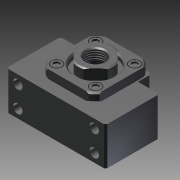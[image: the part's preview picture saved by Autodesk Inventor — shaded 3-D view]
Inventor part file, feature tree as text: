
AUTODESK INVENTOR PART (.ipt)
format: ipt  version: 2011 SP1 (Build 150282100, 282)  size: 373,760 bytes
history: native  units: mm
features: sketch x26, other x14, revolve x12, extrude x9, hole x5, pattern_linear x3, thread x1
ambient origin geometry x8: Origin, YZ Plane, XZ Plane, XY Plane, X Axis, Y Axis, Z Axis, Center Point
bodies: Solid1 (feature_tree)
feature tree (70):
  extrude  "Extrusion1"  Depth=2.5mm TaperAngle=0.0deg
  hole  "Hole1"  [1 undecoded]
  hole  "Hole2"  [1 undecoded]
  hole  "Hole3"  [1 undecoded]
  hole  "Hole4"  [1 undecoded]
  extrude  "Extrusion2"  Depth=20.0mm
  revolve  "Revolution1"  [1 undecoded]
  extrude  "Extrusion3"  Depth=20.0mm
  extrude  "Extrusion4"  TaperAngle=360.0deg  [1 undecoded]
  revolve  "Revolution2"  Angle=360.0deg
  hole  "Hole5"  [1 undecoded]
  revolve  "Revolution3"  Angle=360.0deg
  thread  "Thread1"  [1 undecoded]
  revolve  "Revolution4"  [1 undecoded]
  revolve  "Revolution5"  [1 undecoded]
  pattern_linear  "Rectangular Pattern1"  [2 undecoded]
  revolve  "Revolution6"  [1 undecoded]
  pattern_linear  "Rectangular Pattern2"  [2 undecoded]
  extrude  "Extrusion5"  [1 undecoded]
  pattern_linear  "Rectangular Pattern3"  [2 undecoded]
  revolve  "Revolution7"  [1 undecoded]
  revolve  "Revolution8"  [1 undecoded]
  extrude  "Extrusion6"  [1 undecoded]
  revolve  "Revolution9"  [1 undecoded]
  revolve  "Revolution10"  [1 undecoded]
  extrude  "Extrusion7"  [1 undecoded]
  extrude  "Extrusion8"  [1 undecoded]
  revolve  "Revolution11"  [1 undecoded]
  revolve  "Revolution12"  [1 undecoded]
  extrude  "Extrusion9"  [1 undecoded]
  other  "unit_XY"
  other  "unit_YZ"
  other  "unit_ZX"
  other  "unit_X"
  other  "unit_Y"
  other  "unit_Z"
  other  "unit_Center"
  other  "unit_collar_XY"
  other  "unit_collar_YZ"
  other  "unit_collar_ZX"
  other  "unit_collar_X"
  other  "unit_collar_Y"
  other  "unit_collar_Z"
  other  "unit_collar_Center"
  sketch  "Sketch_1"  dims[d0=27.0mm d1=0.0mm]
  sketch  "Sketch2"  dims[d2=6.6mm d3=6.0mm d4=11.0mm d5=6.5mm d6=90.0deg d7=38.0mm d8=0.0mm]
  sketch  "Sketch3"  dims[d9=6.6mm d10=6.0mm d11=11.0mm d12=6.5mm d13=90.0deg d14=38.0mm d15=0.0mm]
  sketch  "Sketch4"  dims[d16=6.6mm d17=6.0mm d18=11.0mm d19=6.5mm d20=90.0deg d21=38.0mm d22=0.0mm]
  sketch  "Sketch5"  dims[d23=6.6mm d24=6.0mm d25=11.0mm d26=6.5mm d27=90.0deg d28=38.0mm d29=0.0mm d30=2.5mm d31=0.0mm]
  sketch  "Sketch_10"  dims[d32=360.0deg d33=8.5mm d34=0.0mm]
  sketch  "Sketch_13"  dims[d49=360.0deg d50=20.0mm d52=27.577164mm d53=20.0mm d55=27.577164mm]
  sketch  "Sketch_11"  dims[d35=3.5mm d36=0.0mm d37=360.0deg]
  sketch  "Sketch_12"  dims[d46=6.876mm d47=0.0mm d48=360.0deg]
  sketch  "Sketch_14"  dims[d56=360.0deg d57=20.0mm d59=27.577164mm d60=20.0mm d62=27.577164mm]
  sketch  "Sketch11"  dims[d38=15.0mm d39=6.0mm d40=19.5mm d41=6.0mm d42=90.0deg d43=30.0mm d44=0.0mm d45=360.0deg]
  sketch  "Sketch_16"  dims[d63=1.2mm d64=0.0mm d65=20.0mm d67=27.577164mm d68=20.0mm d70=27.577164mm]
  sketch  "Sketch_17"  dims[d71=360.0deg d72=360.0deg]
  sketch  "Sketch_18"  dims[d73=1.2mm d74=0.0mm d75=360.0deg]
  sketch  "Sketch_20"  dims[d76=360.0deg d77=16.0mm d78=0.0mm]
  sketch  "Sketch_22"  dims[d79=6.0mm d80=0.0mm d81=360.0deg d82=360.0deg]
  sketch  "Sketch_24"  dims[d83=0.01mm d84=0.0mm d85=0.0mm d86=0.0mm]
  sketch  "Sketch_25"
  sketch  "Sketch_26"
  sketch  "Sketch_28"
  sketch  "Sketch_29"
  sketch  "Sketch_33"
  sketch  "Sketch_27"
  sketch  "Sketch_30"
  sketch  "Sketch_31"
  sketch  "Sketch_32"
note: 28 required parameter values undecoded (feature->parameter linkage not recoverable at this tier; creation-order binding heuristic only, values carry confidence <= 0.55)